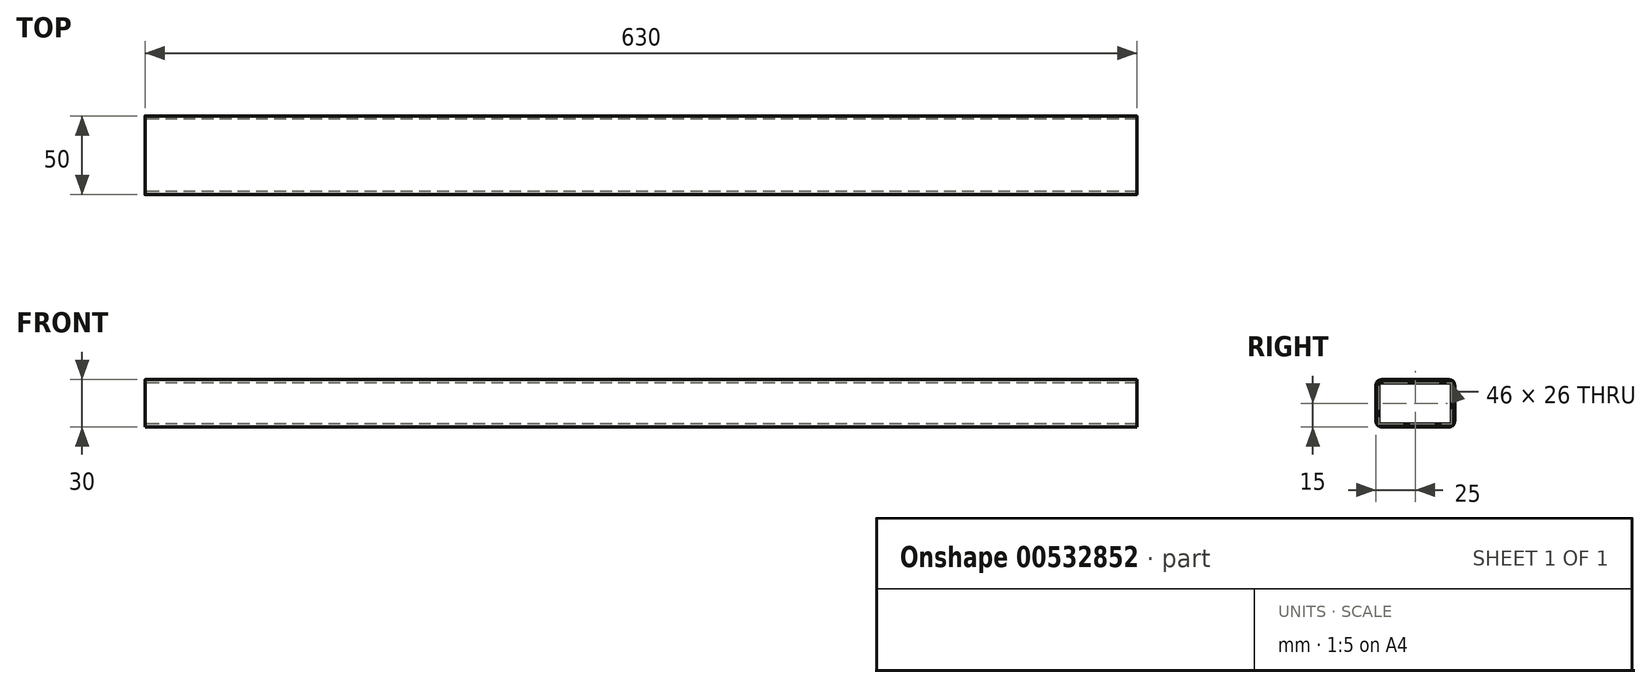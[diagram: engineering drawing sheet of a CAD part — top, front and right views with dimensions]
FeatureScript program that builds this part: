
annotation { "Feature Type Name" : "Feature", "Feature Type Description" : "" }
export const myFeature = defineFeature(function(context is Context, id is Id, definition is map)
    precondition{}
    {
        {
            var Q0;
            Q0=qCreatedBy(makeId("Right.planeOp"),FACE);
            var sketch = newSketch(context, id + "F0", { "sketchPlane" : qUnion([Q0])});
            skLineSegment(sketch, "E0.bottom", {"start": v(21.5, 15) * mm, "end": v(-21.5, 15) * mm});
            skLineSegment(sketch, "E0.top", {"start": v(21.5, -15) * mm, "end": v(-21.5, -15) * mm});
            skLineSegment(sketch, "E0.left", {"start": v(25, 11.5) * mm, "end": v(25, -11.5) * mm});
            skLineSegment(sketch, "E0.right", {"start": v(-25, 11.5) * mm, "end": v(-25, -11.5) * mm});
            skPoint(sketch, "E0.middle", {"position": v(0, 0) * mm});
            skLineSegment(sketch, "E1.bottom", {"start": v(23, 13) * mm, "end": v(-23, 13) * mm});
            skLineSegment(sketch, "E1.top", {"start": v(23, -13) * mm, "end": v(-23, -13) * mm});
            skLineSegment(sketch, "E1.left", {"start": v(23, 13) * mm, "end": v(23, -13) * mm});
            skLineSegment(sketch, "E1.right", {"start": v(-23, 13) * mm, "end": v(-23, -13) * mm});
            skPoint(sketch, "E2.visualSharp", {"position": v(-25, 15) * mm});
            skArc(sketch, "E2.filletArc", {"start": v(-21.5, 15) * mm, "mid": v(-23.97, 13.97) * mm, "end": v(-25, 11.5) * mm});
            skPoint(sketch, "E3.visualSharp", {"position": v(25, 15) * mm});
            skArc(sketch, "E3.filletArc", {"start": v(25, 11.5) * mm, "mid": v(23.97, 13.97) * mm, "end": v(21.5, 15) * mm});
            skPoint(sketch, "E4.visualSharp", {"position": v(25, -15) * mm});
            skArc(sketch, "E4.filletArc", {"start": v(21.5, -15) * mm, "mid": v(23.97, -13.97) * mm, "end": v(25, -11.5) * mm});
            skPoint(sketch, "E5.visualSharp", {"position": v(-25, -15) * mm});
            skArc(sketch, "E5.filletArc", {"start": v(-25, -11.5) * mm, "mid": v(-23.97, -13.97) * mm, "end": v(-21.5, -15) * mm});
            skSolve(sketch);
        }
        {
            var Q0;
            Q0=makeQuery(id+"F0.imprint","IMPRINT",FACE,{"disambiguationData":[TD([[makeQuery(id+"F0.imprint","IMPRINT",EDGE,{"derivedFrom":sQuery(id+"F0.wireOp",EDGE,"E0.bottom")}),1.0]])]});
            extrude(context, id + "F1", {"entities" : qUnion([Q0]), "depth" : 630 * mm, "offsetDistance" : 25 * mm});
        }
    });
